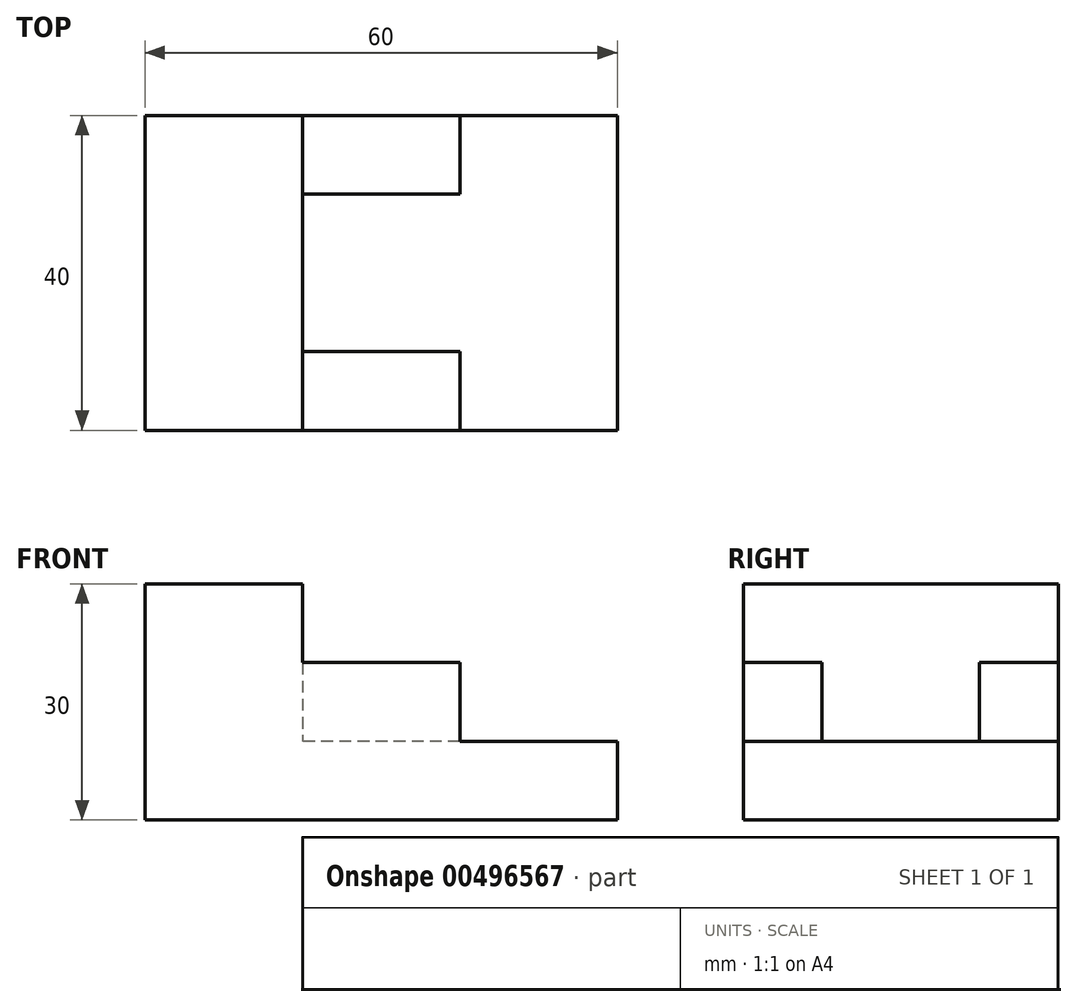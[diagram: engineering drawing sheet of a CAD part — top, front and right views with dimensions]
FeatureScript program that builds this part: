
annotation { "Feature Type Name" : "Feature", "Feature Type Description" : "" }
export const myFeature = defineFeature(function(context is Context, id is Id, definition is map)
    precondition{}
    {
        {
            var Q0;
            Q0=qCreatedBy(makeId("Front.planeOp"),FACE);
            var sketch = newSketch(context, id + "F0", { "sketchPlane" : qUnion([Q0])});
            skLineSegment(sketch, "E0", {"start": v(0, 0) * mm, "end": v(0, 30) * mm});
            skLineSegment(sketch, "E1", {"start": v(0, 0) * mm, "end": v(60, 0) * mm});
            skLineSegment(sketch, "E2", {"start": v(60, 0) * mm, "end": v(60, 10) * mm});
            skLineSegment(sketch, "E3", {"start": v(60, 10) * mm, "end": v(20, 10) * mm});
            skLineSegment(sketch, "E4", {"start": v(20, 10) * mm, "end": v(20, 30) * mm});
            skLineSegment(sketch, "E5", {"start": v(20, 30) * mm, "end": v(0, 30) * mm});
            skSolve(sketch);
        }
        {
            var Q0;
            Q0 = qSketchRegion(id + "F0", true);
            extrude(context, id + "F1", {"entities" : qUnion([Q0]), "depth" : 40 * mm});
        }
        {
            var Q0;
            Q0=makeQuery(id+"F1.opExtrude","SWEPT_FACE",FACE,{"disambiguationData":[OSD([sQuery(id+"F0.wireOp",EDGE,"E3")])]});
            var sketch = newSketch(context, id + "F2", { "sketchPlane" : qUnion([Q0])});
            skLineSegment(sketch, "E6", {"start": v(20, 0) * mm, "end": v(40, 0) * mm});
            skLineSegment(sketch, "E7", {"start": v(40, 0) * mm, "end": v(40, -10) * mm});
            skLineSegment(sketch, "E8", {"start": v(40, -10) * mm, "end": v(20, -10) * mm});
            skLineSegment(sketch, "E9", {"start": v(20, -40) * mm, "end": v(40, -40) * mm});
            skLineSegment(sketch, "E10", {"start": v(40, -40) * mm, "end": v(40, -30) * mm});
            skLineSegment(sketch, "E11", {"start": v(40, -30) * mm, "end": v(20, -30) * mm});
            skSolve(sketch);
        }
        {
            var Q0;
            {var subQ0=sQuery(id+"F2.wireOp",EDGE,"E6");Q0=makeQuery(id+"F2.imprint","IMPRINT",FACE,{"disambiguationData":[TD([[makeQuery(id+"F2.imprint","IMPRINT",EDGE,{"derivedFrom":subQ0}),1.0]])]});}
            var Q1;
            {var subQ0=sQuery(id+"F2.wireOp",EDGE,"E9");Q1=makeQuery(id+"F2.imprint","IMPRINT",FACE,{"disambiguationData":[TD([[makeQuery(id+"F2.imprint","IMPRINT",EDGE,{"derivedFrom":subQ0}),-1.0]])]});}
            extrude(context, id + "F3", {"entities" : qUnion([Q0, Q1]), "operationType" : NewBodyOperationType.ADD, "depth" : 10 * mm});
        }
    });
